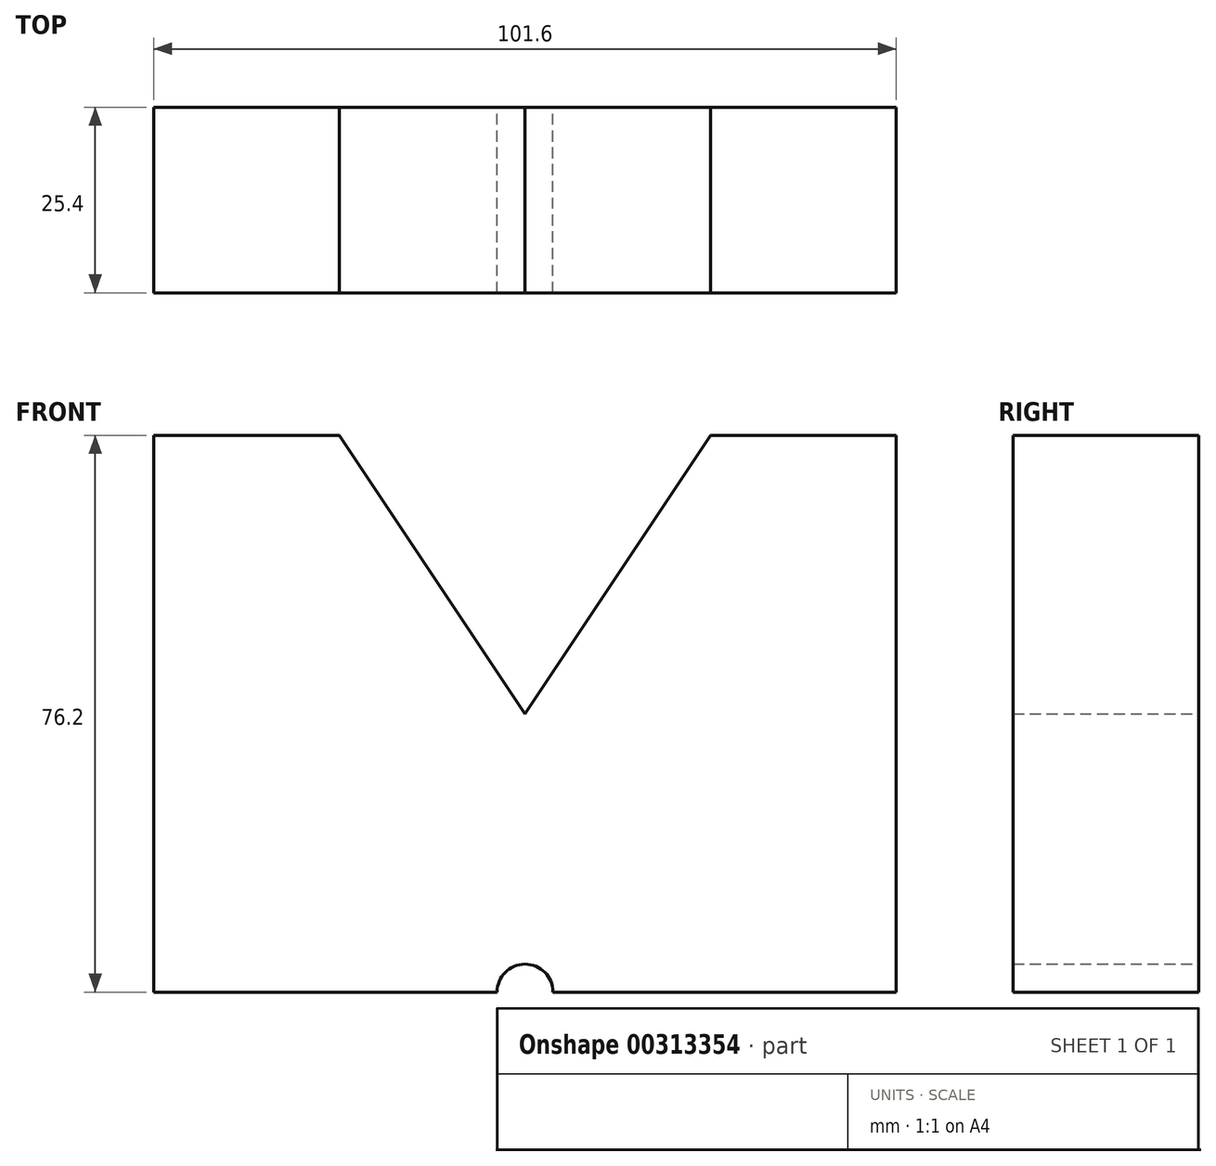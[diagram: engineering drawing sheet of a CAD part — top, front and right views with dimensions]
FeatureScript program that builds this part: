
annotation { "Feature Type Name" : "Feature", "Feature Type Description" : "" }
export const myFeature = defineFeature(function(context is Context, id is Id, definition is map)
    precondition{}
    {
        {
            var Q0;
            Q0=qCreatedBy(makeId("Front.planeOp"),FACE);
            var sketch = newSketch(context, id + "F0", { "sketchPlane" : qUnion([Q0])});
            skLineSegment(sketch, "E0", {"start": v(-48.38, -52.56) * mm, "end": v(53.22, -52.56) * mm});
            skLineSegment(sketch, "E1", {"start": v(53.22, -52.56) * mm, "end": v(53.22, 23.64) * mm});
            skLineSegment(sketch, "E2", {"start": v(53.22, 23.64) * mm, "end": v(27.82, 23.64) * mm});
            skLineSegment(sketch, "E3", {"start": v(-22.98, 23.64) * mm, "end": v(-48.38, 23.64) * mm});
            skLineSegment(sketch, "E4", {"start": v(-48.38, 23.64) * mm, "end": v(-48.38, -52.56) * mm});
            skCircle(sketch, "E5", {"center": v(2.42, -52.56) * mm, "radius": 3.82 * mm});
            skLineSegment(sketch, "E6", {"start": v(2.42, -14.46) * mm, "end": v(27.82, 23.64) * mm});
            skLineSegment(sketch, "E7", {"start": v(-22.98, 23.64) * mm, "end": v(2.42, -14.46) * mm});
            skSolve(sketch);
        }
        {
            var Q0;
            {var subQ0=sQuery(id+"F0.wireOp",EDGE,"E1");Q0=makeQuery(id+"F0.imprint","IMPRINT",FACE,{"disambiguationData":[TD([[makeQuery(id+"F0.imprint","IMPRINT",EDGE,{"derivedFrom":subQ0}),1.0]])]});}
            extrude(context, id + "F1", {"entities" : qUnion([Q0]), "depth" : 25.4 * mm});
        }
    });
